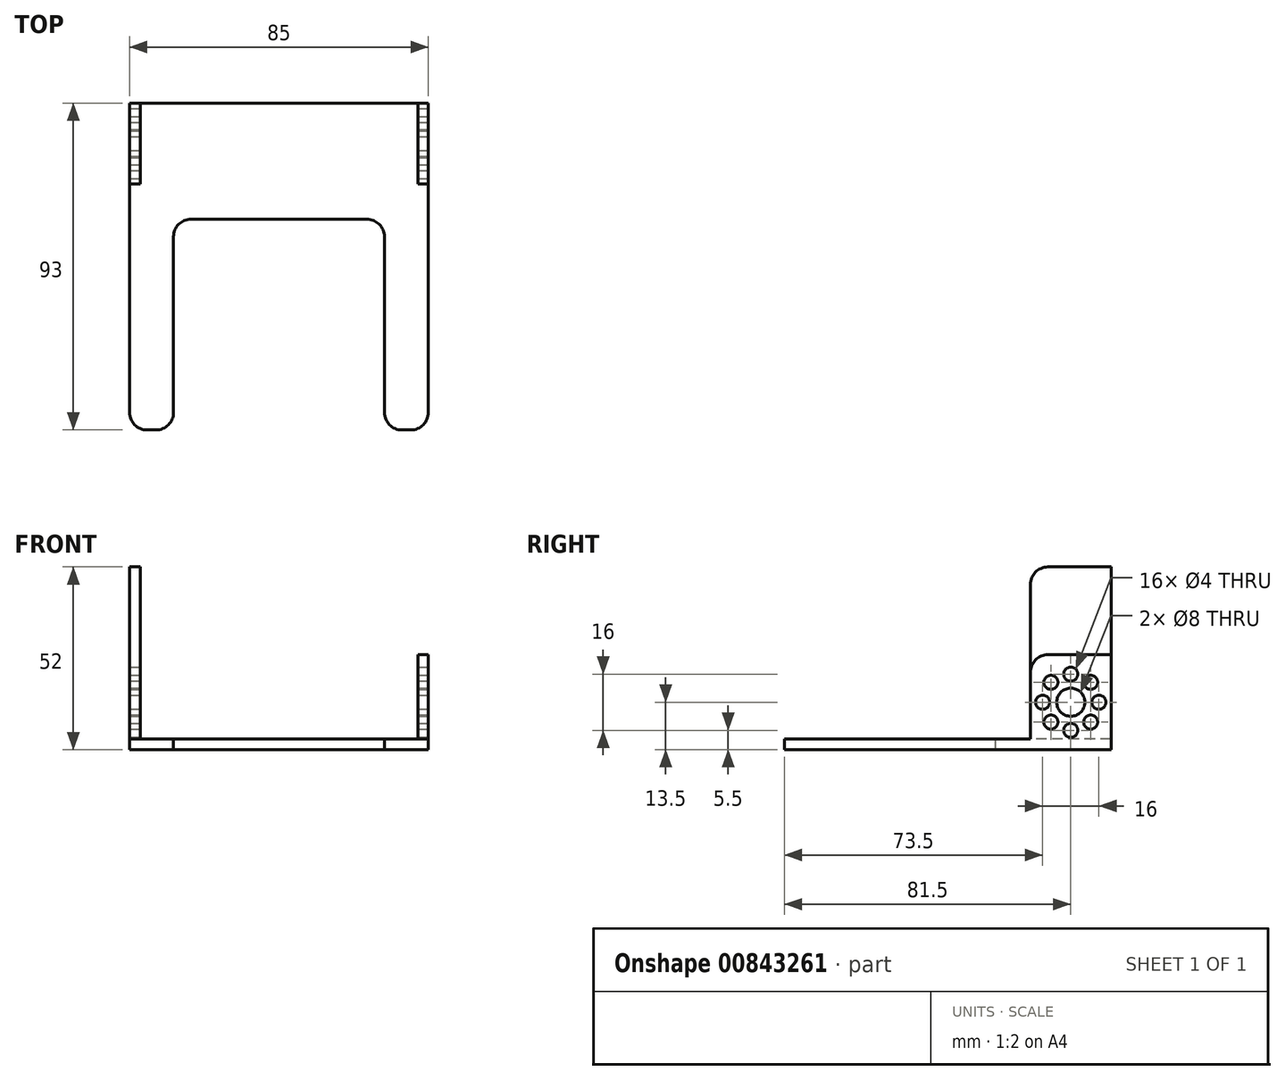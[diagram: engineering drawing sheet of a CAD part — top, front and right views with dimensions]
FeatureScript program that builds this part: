
annotation { "Feature Type Name" : "Feature", "Feature Type Description" : "" }
export const myFeature = defineFeature(function(context is Context, id is Id, definition is map)
    precondition{}
    {
        {
            var Q0;
            Q0=qCreatedBy(makeId("Top.planeOp"),FACE);
            var sketch = newSketch(context, id + "F0", { "sketchPlane" : qUnion([Q0])});
            skLineSegment(sketch, "E0.bottom", {"start": v(0, 0) * mm, "end": v(85, 0) * mm});
            skLineSegment(sketch, "E0.top", {"start": v(0, 23) * mm, "end": v(85, 23) * mm});
            skLineSegment(sketch, "E0.left", {"start": v(0, 0) * mm, "end": v(0, 23) * mm});
            skLineSegment(sketch, "E0.right", {"start": v(85, 0) * mm, "end": v(85, 23) * mm});
            skLineSegment(sketch, "E1.top", {"start": v(17.5, -10) * mm, "end": v(67.5, -10) * mm});
            skLineSegment(sketch, "E1.left", {"start": v(0, 0) * mm, "end": v(0, -10) * mm});
            skLineSegment(sketch, "E1.right", {"start": v(85, 0) * mm, "end": v(85, -10) * mm});
            skLineSegment(sketch, "E2.top", {"start": v(5, -70) * mm, "end": v(7.5, -70) * mm});
            skLineSegment(sketch, "E2.left", {"start": v(0, -10) * mm, "end": v(0, -65) * mm});
            skLineSegment(sketch, "E2.right", {"start": v(12.5, -15) * mm, "end": v(12.5, -65) * mm});
            skLineSegment(sketch, "E3.top", {"start": v(80, -70) * mm, "end": v(77.5, -70) * mm});
            skLineSegment(sketch, "E3.left", {"start": v(85, -10) * mm, "end": v(85, -65) * mm});
            skLineSegment(sketch, "E3.right", {"start": v(72.5, -15) * mm, "end": v(72.5, -65) * mm});
            skPoint(sketch, "E4.visualSharp", {"position": v(12.5, -70) * mm});
            skArc(sketch, "E4.filletArc", {"start": v(7.5, -70) * mm, "mid": v(11.04, -68.54) * mm, "end": v(12.5, -65) * mm});
            skPoint(sketch, "E5.visualSharp", {"position": v(0, -70) * mm});
            skArc(sketch, "E5.filletArc", {"start": v(0, -65) * mm, "mid": v(1.46, -68.54) * mm, "end": v(5, -70) * mm});
            skPoint(sketch, "E6.visualSharp", {"position": v(72.5, -70) * mm});
            skArc(sketch, "E6.filletArc", {"start": v(72.5, -65) * mm, "mid": v(73.96, -68.54) * mm, "end": v(77.5, -70) * mm});
            skPoint(sketch, "E7.visualSharp", {"position": v(85, -70) * mm});
            skArc(sketch, "E7.filletArc", {"start": v(80, -70) * mm, "mid": v(83.54, -68.54) * mm, "end": v(85, -65) * mm});
            skPoint(sketch, "E8.visualSharp", {"position": v(12.5, -10) * mm});
            skArc(sketch, "E8.filletArc", {"start": v(17.5, -10) * mm, "mid": v(13.96, -11.46) * mm, "end": v(12.5, -15) * mm});
            skPoint(sketch, "E9.visualSharp", {"position": v(72.5, -10) * mm});
            skArc(sketch, "E9.filletArc", {"start": v(72.5, -15) * mm, "mid": v(71.04, -11.46) * mm, "end": v(67.5, -10) * mm});
            skSolve(sketch);
        }
        {
            var Q0;
            Q0=qSketchRegion(id+"F0",true);
            extrude(context, id + "F1", {"entities" : qUnion([Q0]), "depth" : 3 * mm, "offsetDistance" : 25 * mm});
        }
        {
            var Q0;
            Q0=makeQuery(id+"F1.opExtrude","CAP_FACE",FACE,{"disambiguationData":[OSD([sQuery(id+"F0.wireOp",EDGE,"E0.bottom"),sQuery(id+"F0.wireOp",EDGE,"E0.top"),sQuery(id+"F0.wireOp",EDGE,"E0.left"),sQuery(id+"F0.wireOp",EDGE,"E0.right")])],"isStart":false});
            var sketch = newSketch(context, id + "F2", { "sketchPlane" : qUnion([Q0])});
            skLineSegment(sketch, "E10.bottom", {"start": v(0, 23) * mm, "end": v(3, 23) * mm});
            skLineSegment(sketch, "E10.top", {"start": v(0, 0) * mm, "end": v(3, 0) * mm});
            skLineSegment(sketch, "E10.left", {"start": v(0, 23) * mm, "end": v(0, 0) * mm});
            skLineSegment(sketch, "E10.right", {"start": v(3, 23) * mm, "end": v(3, 0) * mm});
            skLineSegment(sketch, "E11.bottom", {"start": v(85, 23) * mm, "end": v(82, 23) * mm});
            skLineSegment(sketch, "E11.top", {"start": v(85, 0) * mm, "end": v(82, 0) * mm});
            skLineSegment(sketch, "E11.left", {"start": v(85, 23) * mm, "end": v(85, 0) * mm});
            skLineSegment(sketch, "E11.right", {"start": v(82, 23) * mm, "end": v(82, 0) * mm});
            skSolve(sketch);
        }
        {
            var Q0;
            Q0=qSketchRegion(id+"F2",true);
            extrude(context, id + "F3", {"entities" : qUnion([Q0]), "operationType" : NewBodyOperationType.ADD, "depth" : 24 * mm, "offsetDistance" : 25 * mm});
        }
        {
            var Q0;
            Q0=makeQuery(id+"F3.opExtrude","CAP_FACE",FACE,{"disambiguationData":[OSD([sQuery(id+"F2.wireOp",EDGE,"E10.bottom"),sQuery(id+"F2.wireOp",EDGE,"E10.top"),sQuery(id+"F2.wireOp",EDGE,"E10.left"),sQuery(id+"F2.wireOp",EDGE,"E10.right")])],"isStart":false});
            var sketch = newSketch(context, id + "F4", { "sketchPlane" : qUnion([Q0])});
            skLineSegment(sketch, "E12.bottom", {"start": v(0, 23) * mm, "end": v(3, 23) * mm});
            skLineSegment(sketch, "E12.top", {"start": v(0, 0) * mm, "end": v(3, 0) * mm});
            skLineSegment(sketch, "E12.left", {"start": v(0, 23) * mm, "end": v(0, 0) * mm});
            skLineSegment(sketch, "E12.right", {"start": v(3, 23) * mm, "end": v(3, 0) * mm});
            skSolve(sketch);
        }
        {
            var Q0;
            Q0=qSketchRegion(id+"F4",true);
            extrude(context, id + "F5", {"entities" : qUnion([Q0]), "operationType" : NewBodyOperationType.ADD, "depth" : 25 * mm, "offsetDistance" : 25 * mm});
        }
        {
            var Q0;
            Q0=makeQuery(id+"F3.boolean.opBoolean","MERGE",FACE,{"derivedFrom":[makeQuery(id+"F1.opExtrude","SWEPT_FACE",FACE,{"disambiguationData":[OSD([sQuery(id+"F0.wireOp",EDGE,"E0.right"),sQuery(id+"F0.wireOp",EDGE,"E1.right"),sQuery(id+"F0.wireOp",EDGE,"E3.left")])]}),makeQuery(id+"F3.opExtrude","SWEPT_FACE",FACE,{"disambiguationData":[OSD([sQuery(id+"F2.wireOp",EDGE,"E11.left")])]})]});
            var sketch = newSketch(context, id + "F6", { "sketchPlane" : qUnion([Q0])});
            skLineSegment(sketch, "E13", {"start": v(23, 0) * mm, "end": v(23, 27) * mm, "construction": true});
            skCircle(sketch, "E14", {"center": v(11.5, 13.5) * mm, "radius": 4 * mm});
            skCircle(sketch, "E15", {"center": v(19.5, 13.5) * mm, "radius": 2 * mm});
            skPoint(sketch, "E16.orphan", {"position": v(0, 27) * mm});
            skCircle(sketch, "E17.1.0", {"center": v(17.16, 19.16) * mm, "radius": 2 * mm});
            skCircle(sketch, "E17.2.0", {"center": v(11.5, 21.5) * mm, "radius": 2 * mm});
            skCircle(sketch, "E17.3.0", {"center": v(5.84, 19.16) * mm, "radius": 2 * mm});
            skCircle(sketch, "E17.4.0", {"center": v(3.5, 13.5) * mm, "radius": 2 * mm});
            skCircle(sketch, "E17.5.0", {"center": v(5.84, 7.84) * mm, "radius": 2 * mm});
            skCircle(sketch, "E17.6.0", {"center": v(11.5, 5.5) * mm, "radius": 2 * mm});
            skCircle(sketch, "E17.7.0", {"center": v(17.16, 7.84) * mm, "radius": 2 * mm});
            skSolve(sketch);
        }
        {
            var Q0;
            Q0 = qSketchRegion(id + "F6", true);
            extrude(context, id + "F7", {"entities" : qUnion([Q0]), "operationType" : NewBodyOperationType.REMOVE, "oppositeDirection" : true, "depth" : 100 * mm, "offsetDistance" : 25 * mm});
        }
        {
            var Q0;
            Q0=makeQuery(id+"F5.opExtrude","CAP_EDGE",EDGE,{"disambiguationData":[OSD([sQuery(id+"F4.wireOp",EDGE,"E12.top")])],"isStart":false});
            var Q1;
            Q1=makeQuery(id+"F3.opExtrude","CAP_EDGE",EDGE,{"disambiguationData":[OSD([sQuery(id+"F2.wireOp",EDGE,"E11.top")])],"isStart":false});
            fillet(context, id + "F8", {"entities" : qUnion([Q0, Q1]), "radius" : 5 * mm, "tangentPropagation" : true, "allowEdgeOverflow" : false});
        }
    });
